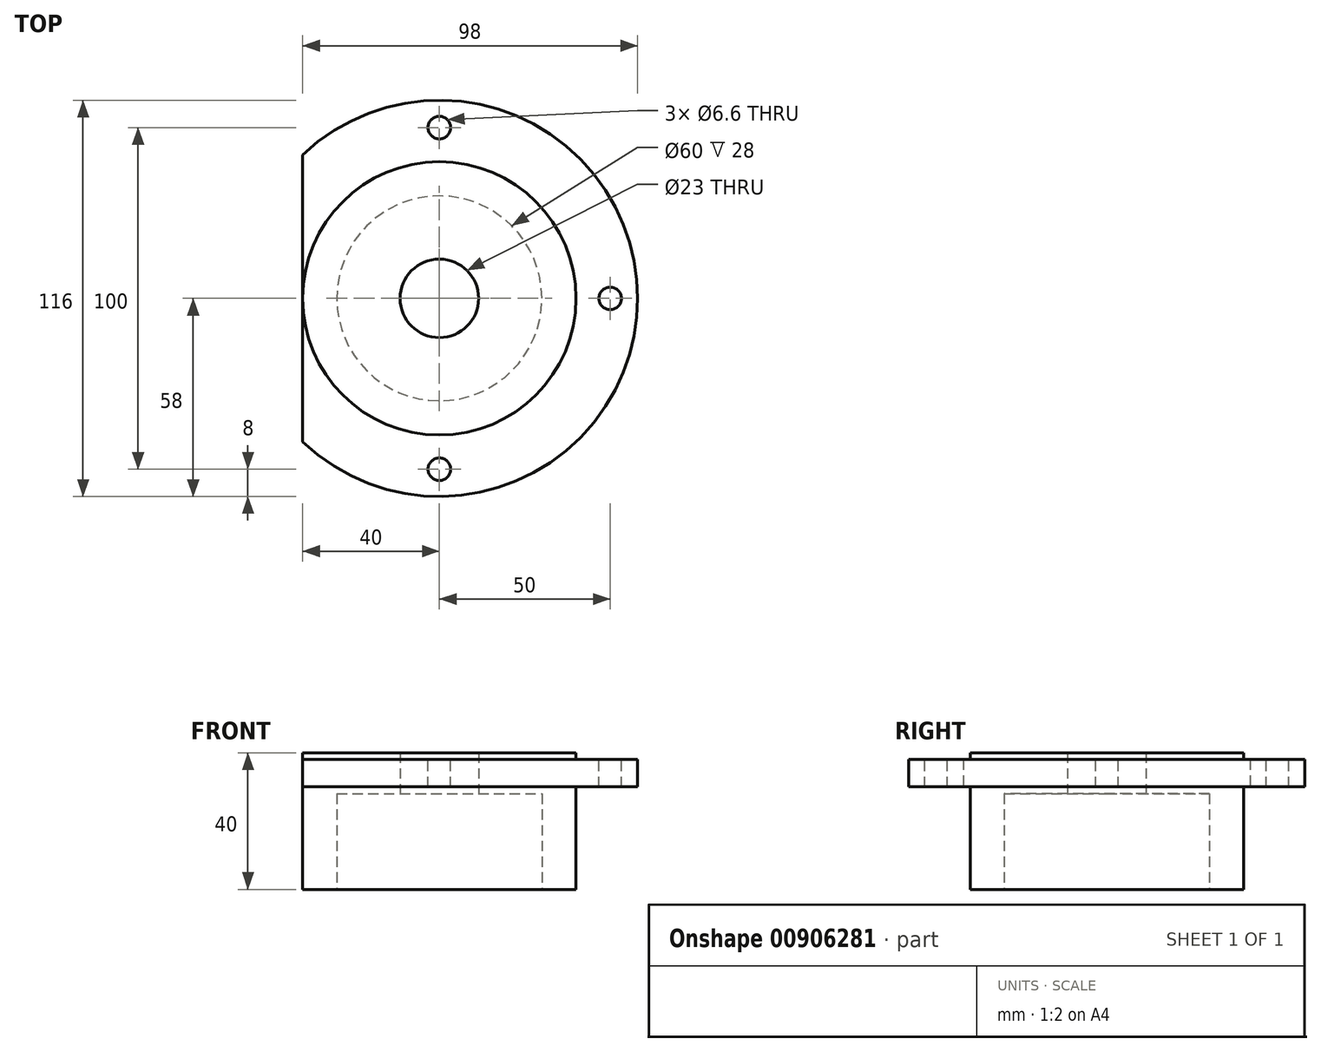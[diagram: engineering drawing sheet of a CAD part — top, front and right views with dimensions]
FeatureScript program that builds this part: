
annotation { "Feature Type Name" : "Feature", "Feature Type Description" : "" }
export const myFeature = defineFeature(function(context is Context, id is Id, definition is map)
    precondition{}
    {
        {
            var Q0;
            Q0=qCreatedBy(makeId("Right.planeOp"),FACE);
            var sketch = newSketch(context, id + "F0", { "sketchPlane" : qUnion([Q0])});
            skLineSegment(sketch, "E0", {"start": v(-58, 40) * mm, "end": v(-11.5, 40) * mm});
            skLineSegment(sketch, "E1", {"start": v(-11.5, 40) * mm, "end": v(-11.5, 28) * mm});
            skLineSegment(sketch, "E2", {"start": v(-11.5, 28) * mm, "end": v(-30, 28) * mm});
            skLineSegment(sketch, "E3", {"start": v(-30, 28) * mm, "end": v(-30, 0) * mm});
            skLineSegment(sketch, "E4", {"start": v(-58, 40) * mm, "end": v(-58, 30) * mm});
            skLineSegment(sketch, "E5", {"start": v(-58, 30) * mm, "end": v(-40, 30) * mm});
            skLineSegment(sketch, "E6", {"start": v(-40, 30) * mm, "end": v(-40, 0) * mm});
            skLineSegment(sketch, "E7", {"start": v(-40, 0) * mm, "end": v(-30, 0) * mm});
            skLineSegment(sketch, "E8", {"start": v(0, 0) * mm, "end": v(0, 65.11) * mm});
            skLineSegment(sketch, "E9", {"start": v(-40, 40) * mm, "end": v(-40, 38) * mm});
            skLineSegment(sketch, "E10", {"start": v(-40, 38) * mm, "end": v(-58, 38) * mm});
            skSolve(sketch);
        }
        {
            var Q0;
            {var subQ0=sQuery(id+"F0.wireOp",EDGE,"E1");Q0=makeQuery(id+"F0.imprint","IMPRINT",FACE,{"disambiguationData":[TD([[makeQuery(id+"F0.imprint","IMPRINT",EDGE,{"derivedFrom":subQ0}),-1.0]])]});}
            var Q1;
            Q1=sQuery(id+"F0.wireOp",EDGE,"E8");
            revolve(context, id + "F1", {"surfaceOperationType" : NewSurfaceOperationType.NEW, "entities" : qUnion([Q0]), "axis" : qUnion([Q1]), "revolveType" : RevolveType.FULL});
        }
        {
            var Q0;
            Q0=makeQuery(id+"F1.opRevolve","SWEPT_FACE",FACE,{"disambiguationData":[OSD([sQuery(id+"F0.wireOp",EDGE,"E0")])]});
            var sketch = newSketch(context, id + "F2", { "sketchPlane" : qUnion([Q0])});
            skPoint(sketch, "E11", {"position": v(-50, 0) * mm});
            skPoint(sketch, "E12.1.0", {"position": v(0, -50) * mm});
            skPoint(sketch, "E12.2.0", {"position": v(50, 0) * mm});
            skPoint(sketch, "E12.3.0", {"position": v(0, 50) * mm});
            skPoint(sketch, "E12.center", {"position": v(0, 0) * mm});
            skSolve(sketch);
        }
        {
            var Q0;
            Q0=sQuery(id+"F2.wireOp",VERTEX,"E11");
            var Q1;
            Q1=sQuery(id+"F2.wireOp",VERTEX,"E12.5.0");
            var Q2;
            Q2=sQuery(id+"F2.wireOp",VERTEX,"E12.4.0");
            var Q3;
            Q3=sQuery(id+"F2.wireOp",VERTEX,"E12.3.0");
            var Q4;
            Q4=sQuery(id+"F2.wireOp",VERTEX,"E12.2.0");
            var Q5;
            Q5=sQuery(id+"F2.wireOp",VERTEX,"E12.1.0");
            var Q6;
            Q6=makeQuery(id+"F1.opRevolve","SWEPT_BODY",BODY,{"disambiguationData":[OSD([sQuery(id+"F0.wireOp",EDGE,"E0"),sQuery(id+"F0.wireOp",EDGE,"E1"),sQuery(id+"F0.wireOp",EDGE,"E2"),sQuery(id+"F0.wireOp",EDGE,"E3"),sQuery(id+"F0.wireOp",EDGE,"E4"),sQuery(id+"F0.wireOp",EDGE,"E5"),sQuery(id+"F0.wireOp",EDGE,"E6"),sQuery(id+"F0.wireOp",EDGE,"E7")])]});
            hole(context, id + "F3", {"style" : HoleStyle.SIMPLE, "endStyle" : HoleEndStyle.THROUGH, "standardTappedOrClearance" : lookupTablePath({ "fit" : "Normal", "standard" : "ISO", "size" : "M6", "type" : "Clearance" }), "standardBlindInLast" : lookupTablePath({ "fit" : "Normal", "standard" : "ISO", "size" : "M6", "type" : "Clearance" }), "holeDiameter" : 6.6 * mm, "majorDiameter" : 5 * mm, "isTappedThrough" : true, "tappedDepth" : 12 * mm, "tapClearance" : 3, "locations" : qUnion([Q0, Q1, Q2, Q3, Q4, Q5]), "scope" : qUnion([Q6])});
        }
        {
            var Q0;
            Q0=makeQuery(id+"F1.opRevolve","SWEPT_FACE",FACE,{"disambiguationData":[OSD([sQuery(id+"F0.wireOp",EDGE,"E10")])]});
            var sketch = newSketch(context, id + "F4", { "sketchPlane" : qUnion([Q0])});
            skLineSegment(sketch, "E13.bottom", {"start": v(-40, 0) * mm, "end": v(-66.53, 0) * mm});
            skLineSegment(sketch, "E13.top", {"start": v(-40, -44.47) * mm, "end": v(-66.53, -44.47) * mm});
            skLineSegment(sketch, "E13.left", {"start": v(-40, 0) * mm, "end": v(-40, -44.47) * mm});
            skLineSegment(sketch, "E13.right", {"start": v(-66.53, 0) * mm, "end": v(-66.53, -44.47) * mm});
            skLineSegment(sketch, "E14.top", {"start": v(-40, 51.6) * mm, "end": v(-66.53, 51.6) * mm});
            skLineSegment(sketch, "E14.left", {"start": v(-40, 0) * mm, "end": v(-40, 51.6) * mm});
            skLineSegment(sketch, "E14.right", {"start": v(-66.53, 0) * mm, "end": v(-66.53, 51.6) * mm});
            skSolve(sketch);
        }
        {
            var Q0;
            {var subQ2=sQuery(id+"F4.wireOp",EDGE,"E14.top");Q0=makeQuery(id+"F4.imprint","IMPRINT",FACE,{"disambiguationData":[TD([[makeQuery(id+"F4.imprint","IMPRINT",EDGE,{"derivedFrom":subQ2}),1.0]])]});}
            var Q1;
            {var subQ1=sQuery(id+"F0.wireOp",EDGE,"E10");var subQ4=sQuery(id+"F4.wireOp",EDGE,"E13.bottom");var subQ6=makeQuery(id+"F3.hole-0.boolean.opBoolean","INTERSECT",EDGE,{"derivedFrom":[makeQuery(id+"F1.opRevolve","SWEPT_FACE",FACE,{"disambiguationData":[OSD([subQ1])]}),makeQuery(id+"F3.hole-0.opRevolve","SWEPT_FACE",FACE,{"disambiguationData":[OSD([sQuery(id+"F3.hole-0.sketch.wireOp",EDGE,"core_line_2")])]})]});var subQ7=makeQuery(id+"F4.imprint","INTERSECT",VERTEX,{"disambiguationData":[OD(1.0)],"derivedFrom":[subQ6,subQ4]});Q1=makeQuery(id+"F4.imprint","IMPRINT",FACE,{"disambiguationData":[TD([[makeQuery(id+"F4.imprint","IMPRINT",EDGE,{"disambiguationData":[TD([[subQ7,-1.0]])],"derivedFrom":subQ4}),-1.0]])]});}
            var Q2;
            {var subQ1=sQuery(id+"F0.wireOp",EDGE,"E10");var subQ4=sQuery(id+"F4.wireOp",EDGE,"E13.bottom");var subQ6=makeQuery(id+"F3.hole-0.boolean.opBoolean","INTERSECT",EDGE,{"derivedFrom":[makeQuery(id+"F1.opRevolve","SWEPT_FACE",FACE,{"disambiguationData":[OSD([subQ1])]}),makeQuery(id+"F3.hole-0.opRevolve","SWEPT_FACE",FACE,{"disambiguationData":[OSD([sQuery(id+"F3.hole-0.sketch.wireOp",EDGE,"core_line_2")])]})]});var subQ7=makeQuery(id+"F4.imprint","INTERSECT",VERTEX,{"disambiguationData":[OD(1.0)],"derivedFrom":[subQ6,subQ4]});Q2=makeQuery(id+"F4.imprint","IMPRINT",FACE,{"disambiguationData":[TD([[makeQuery(id+"F4.imprint","IMPRINT",EDGE,{"disambiguationData":[TD([[subQ7,-1.0]])],"derivedFrom":subQ4}),1.0]])]});}
            var Q3;
            {var subQ5=sQuery(id+"F4.wireOp",EDGE,"E13.top");Q3=makeQuery(id+"F4.imprint","IMPRINT",FACE,{"disambiguationData":[TD([[makeQuery(id+"F4.imprint","IMPRINT",EDGE,{"derivedFrom":subQ5}),-1.0]])]});}
            extrude(context, id + "F5", {"entities" : qUnion([Q0, Q1, Q2, Q3]), "operationType" : NewBodyOperationType.REMOVE, "oppositeDirection" : true, "depth" : 25 * mm, "offsetDistance" : 25 * mm});
        }
    });
